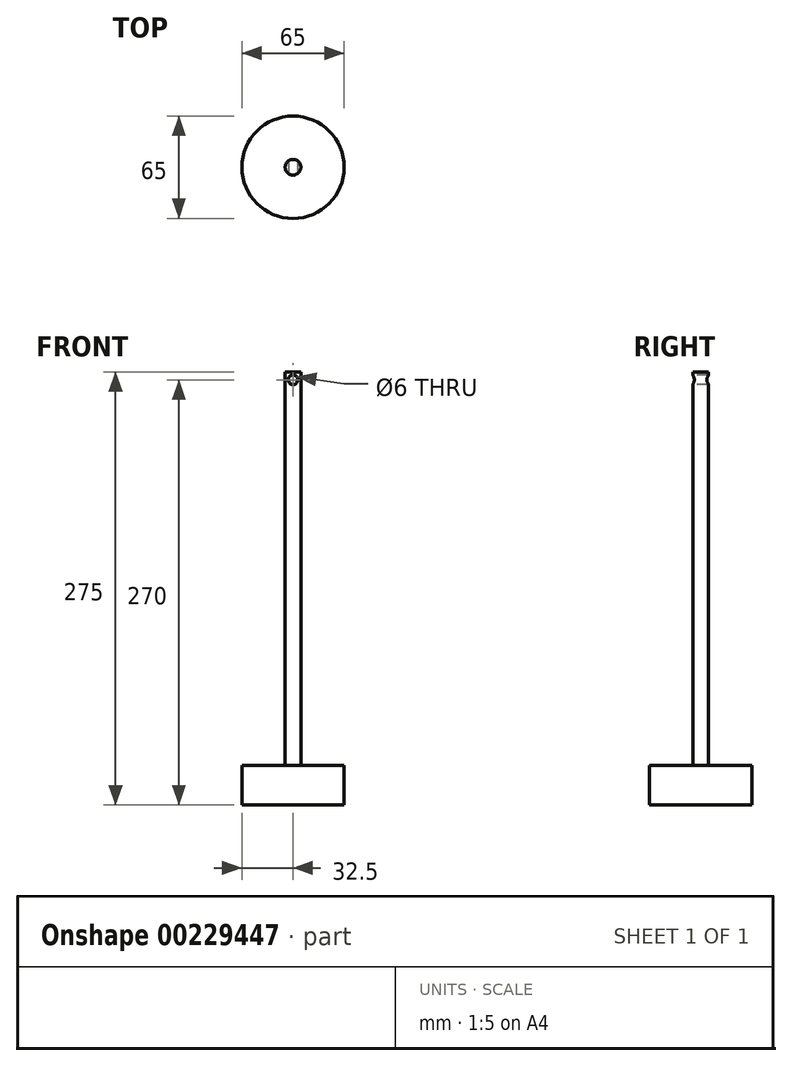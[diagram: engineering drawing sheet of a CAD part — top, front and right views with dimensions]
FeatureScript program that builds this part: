
annotation { "Feature Type Name" : "Feature", "Feature Type Description" : "" }
export const myFeature = defineFeature(function(context is Context, id is Id, definition is map)
    precondition{}
    {
        {
            var Q0;
            Q0=qCreatedBy(makeId("Top.planeOp"),FACE);
            var sketch = newSketch(context, id + "F0", { "sketchPlane" : qUnion([Q0])});
            skCircle(sketch, "E0", {"center": v(0, 0) * mm, "radius": 32.5 * mm});
            skSolve(sketch);
        }
        {
            var Q0;
            Q0=makeQuery(id+"F0.imprint","IMPRINT",FACE,{"disambiguationData":[TD([[makeQuery(id+"F0.imprint","IMPRINT",EDGE,{"derivedFrom":sQuery(id+"F0.wireOp",EDGE,"E0")}),1.0]])]});
            extrude(context, id + "F1", {"entities" : qUnion([Q0]), "depth" : 25 * mm});
        }
        {
            var Q0;
            Q0=makeQuery(id+"F1.opExtrude","CAP_FACE",FACE,{"disambiguationData":[OSD([sQuery(id+"F0.wireOp",EDGE,"E0")])],"isStart":false});
            var sketch = newSketch(context, id + "F2", { "sketchPlane" : qUnion([Q0])});
            skCircle(sketch, "E1", {"center": v(0, 0) * mm, "radius": 5 * mm});
            skSolve(sketch);
        }
        {
            var Q0;
            Q0=makeQuery(id+"F2.imprint","IMPRINT",FACE,{"disambiguationData":[TD([[makeQuery(id+"F2.imprint","IMPRINT",EDGE,{"derivedFrom":sQuery(id+"F2.wireOp",EDGE,"E1")}),1.0]])]});
            extrude(context, id + "F3", {"entities" : qUnion([Q0]), "operationType" : NewBodyOperationType.ADD, "depth" : 250 * mm});
        }
        {
            var Q0;
            Q0=qCreatedBy(makeId("Front.planeOp"),FACE);
            var sketch = newSketch(context, id + "F4", { "sketchPlane" : qUnion([Q0])});
            skLineSegment(sketch, "E2.0", {"start": v(-5, 275) * mm, "end": v(5, 275) * mm, "construction": true});
            skLineSegment(sketch, "E3", {"start": v(0, 275) * mm, "end": v(0, 259.47) * mm, "construction": true});
            skPoint(sketch, "E3.endSnap0", {"position": v(0, 275) * mm});
            skCircle(sketch, "E4", {"center": v(0, 270) * mm, "radius": 3 * mm});
            skSolve(sketch);
        }
        {
            var Q0;
            Q0=makeQuery(id+"F4.imprint","IMPRINT",FACE,{"disambiguationData":[TD([[makeQuery(id+"F4.imprint","IMPRINT",EDGE,{"derivedFrom":sQuery(id+"F4.wireOp",EDGE,"E4")}),1.0]])]});
            extrude(context, id + "F5", {"entities" : qUnion([Q0]), "operationType" : NewBodyOperationType.REMOVE, "endBound" : BoundingType.SYMMETRIC, "oppositeDirection" : true, "depth" : 25 * mm});
        }
    });
